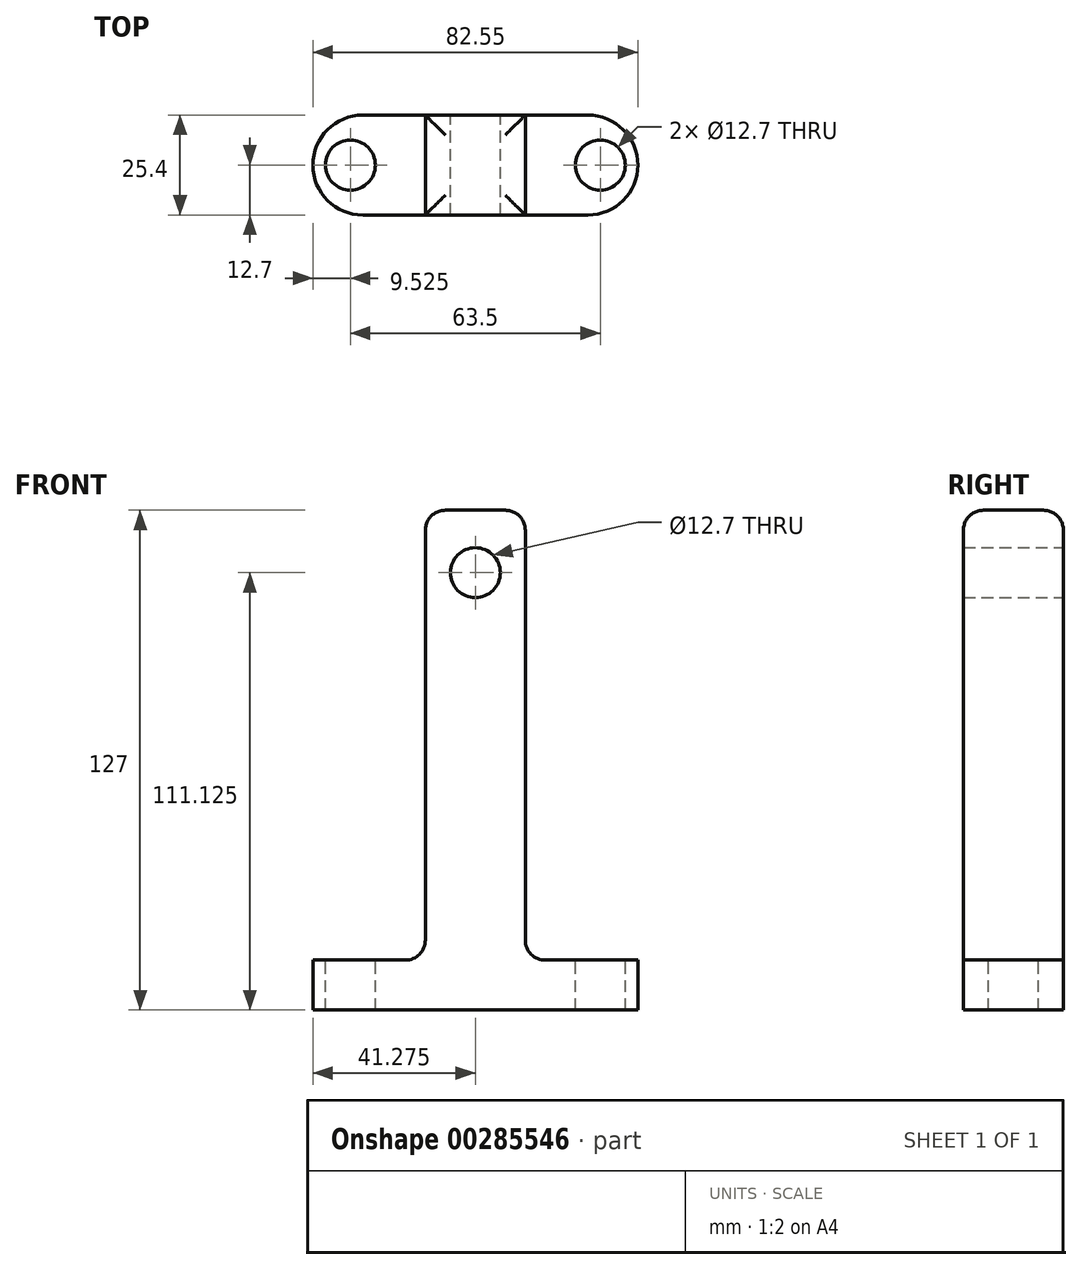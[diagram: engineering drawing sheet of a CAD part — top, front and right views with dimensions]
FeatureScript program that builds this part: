
annotation { "Feature Type Name" : "Feature", "Feature Type Description" : "" }
export const myFeature = defineFeature(function(context is Context, id is Id, definition is map)
    precondition{}
    {
        {
            var Q0;
            Q0=qCreatedBy(makeId("Top.planeOp"),FACE);
            var sketch = newSketch(context, id + "F0", { "sketchPlane" : qUnion([Q0])});
            skLineSegment(sketch, "E0", {"start": v(0, 0) * mm, "end": v(57.15, 0) * mm});
            skLineSegment(sketch, "E1.0", {"start": v(0, -25.4) * mm, "end": v(57.15, -25.4) * mm});
            skArc(sketch, "E2", {"start": v(0, 0) * mm, "mid": v(-12.7, -12.7) * mm, "end": v(0, -25.4) * mm});
            skPoint(sketch, "E2.third.point", {"position": v(12.41, -10) * mm});
            skArc(sketch, "E3", {"start": v(57.15, -25.4) * mm, "mid": v(69.85, -12.7) * mm, "end": v(57.15, 0) * mm});
            skPoint(sketch, "E3.third.point", {"position": v(44.45, -12.67) * mm});
            skLineSegment(sketch, "E4", {"start": v(28.58, 0) * mm, "end": v(28.58, -25.4) * mm, "construction": true});
            skLineSegment(sketch, "E5", {"start": v(15.88, 0) * mm, "end": v(15.88, -25.4) * mm});
            skLineSegment(sketch, "E6.MirrorCS", {"start": v(41.28, 0) * mm, "end": v(41.28, -25.4) * mm});
            skSolve(sketch);
        }
        {
            var Q0;
            Q0 = qSketchRegion(id + "F0", true);
            extrude(context, id + "F1", {"entities" : qUnion([Q0]), "depth" : 12.7 * mm});
        }
        {
            var Q0;
            Q0=qCreatedBy(makeId("Top.planeOp"),FACE);
            cPlane(context, id + "F2", {"entities" : qUnion([Q0]), "cplaneType" : CPlaneType.OFFSET, "offset" : 127 * mm, "width" : 152.4 * mm, "height" : 152.4 * mm});
        }
        {
            var Q0;
            Q0=qCreatedBy(id+"F2.planeOp",FACE);
            var sketch = newSketch(context, id + "F3", { "sketchPlane" : qUnion([Q0])});
            skLineSegment(sketch, "E7", {"start": v(15.88, 0) * mm, "end": v(15.88, -25.4) * mm});
            skPoint(sketch, "E8.orphan", {"position": v(11.05, -22.86) * mm});
            skPoint(sketch, "E9.orphan", {"position": v(15.88, -25.4) * mm});
            skPoint(sketch, "E10.orphan", {"position": v(11.05, -2.54) * mm});
            skPoint(sketch, "E11.orphan", {"position": v(15.88, 0) * mm});
            skLineSegment(sketch, "E12.MirrorCS", {"start": v(41.28, 0) * mm, "end": v(41.28, -25.4) * mm});
            skLineSegment(sketch, "E13", {"start": v(41.28, 0) * mm, "end": v(15.88, 0) * mm});
            skLineSegment(sketch, "E14", {"start": v(15.88, -25.4) * mm, "end": v(41.28, -25.4) * mm});
            skSolve(sketch);
        }
        {
            var Q1;
            {var subQ0=sQuery(id+"F0.wireOp",EDGE,"E5");Q1=makeQuery(id+"F0.imprint","IMPRINT",FACE,{"disambiguationData":[TD([[makeQuery(id+"F0.imprint","IMPRINT",EDGE,{"derivedFrom":subQ0}),1.0]])]});}
            var Q2;
            Q2=makeQuery(id+"F3.imprint","IMPRINT",FACE,{"disambiguationData":[TD([[makeQuery(id+"F3.imprint","IMPRINT",EDGE,{"derivedFrom":sQuery(id+"F3.wireOp",EDGE,"E7")}),1.0]])]});
            loft(context, id + "F4", {"operationType" : NewBodyOperationType.ADD, "sheetProfilesArray" : [{ "sheetProfileEntities" : qUnion([Q1]) }, { "sheetProfileEntities" : qUnion([Q2]) }]});
        }
        {
            var Q0;
            {var subQ0=sQuery(id+"F0.wireOp",EDGE,"E1.0");var subQ1=sQuery(id+"F0.wireOp",EDGE,"E0");Q0=makeQuery(id+"F4.boolean.opBoolean","INTERSECT",EDGE,{"derivedFrom":[makeQuery(id+"F1.opExtrude","CAP_FACE",FACE,{"disambiguationData":[OSD([subQ1,subQ0,sQuery(id+"F0.wireOp",EDGE,"E2"),sQuery(id+"F0.wireOp",EDGE,"E3")])],"isStart":false}),makeQuery(id+"F4.opLoft","SWEPT_FACE",FACE,{"disambiguationData":[OSD([subQ1,subQ0,sQuery(id+"F0.wireOp",EDGE,"E6.MirrorCS"),sQuery(id+"F3.wireOp",EDGE,"E12.MirrorCS"),sQuery(id+"F3.wireOp",EDGE,"E13"),sQuery(id+"F3.wireOp",EDGE,"E14")])]})]});}
            var Q1;
            {var subQ0=sQuery(id+"F0.wireOp",EDGE,"E1.0");var subQ1=sQuery(id+"F0.wireOp",EDGE,"E0");Q1=makeQuery(id+"F4.boolean.opBoolean","INTERSECT",EDGE,{"derivedFrom":[makeQuery(id+"F1.opExtrude","CAP_FACE",FACE,{"disambiguationData":[OSD([subQ1,subQ0,sQuery(id+"F0.wireOp",EDGE,"E2"),sQuery(id+"F0.wireOp",EDGE,"E3")])],"isStart":false}),makeQuery(id+"F4.opLoft","SWEPT_FACE",FACE,{"disambiguationData":[OSD([subQ1,subQ0,sQuery(id+"F0.wireOp",EDGE,"E5"),sQuery(id+"F3.wireOp",EDGE,"E7"),sQuery(id+"F3.wireOp",EDGE,"E13"),sQuery(id+"F3.wireOp",EDGE,"E14")])]})]});}
            var Q2;
            Q2=makeQuery(id+"F4.opLoft","MID_CAP_EDGE",EDGE,{"disambiguationData":[OSD([sQuery(id+"F3.wireOp",EDGE,"E7"),sQuery(id+"F3.wireOp",EDGE,"E12.MirrorCS"),sQuery(id+"F3.wireOp",EDGE,"E13")])],"capPos":1.0});
            var Q3;
            Q3=makeQuery(id+"F4.opLoft","CAP_FACE",FACE,{"disambiguationData":[OSD([makeQuery(id+"F3.imprint","IMPRINT",FACE,{"disambiguationData":[TD([[makeQuery(id+"F3.imprint","IMPRINT",EDGE,{"derivedFrom":sQuery(id+"F3.wireOp",EDGE,"E7")}),1.0]])]})])],"isStart":true});
            fillet(context, id + "F5", {"entities" : qUnion([Q0, Q1, Q2, Q3]), "radius" : 5.08 * mm, "tangentPropagation" : true, "allowEdgeOverflow" : false});
        }
        {
            var Q0;
            Q0=qCreatedBy(makeId("Front.planeOp"),FACE);
            var sketch = newSketch(context, id + "F6", { "sketchPlane" : qUnion([Q0])});
            skPoint(sketch, "E15", {"position": v(0, 111.13) * mm});
            skPoint(sketch, "E16", {"position": v(28.57, 111.13) * mm});
            skSolve(sketch);
        }
        {
            var Q0;
            Q0=sQuery(id+"F6.wireOp",VERTEX,"E16");
            var Q1;
            Q1=makeQuery(id+"F1.opExtrude","SWEPT_BODY",BODY,{"disambiguationData":[OSD([sQuery(id+"F0.wireOp",EDGE,"E0"),sQuery(id+"F0.wireOp",EDGE,"E1.0"),sQuery(id+"F0.wireOp",EDGE,"E2"),sQuery(id+"F0.wireOp",EDGE,"E3")])]});
            hole(context, id + "F7", {"style" : HoleStyle.SIMPLE, "endStyle" : HoleEndStyle.BLIND, "oppositeDirection" : true, "holeDiameter" : 12.7 * mm, "holeDepth" : 25.4 * mm, "tappedDepth" : 12.7 * mm, "tapClearance" : 3, "locations" : qUnion([Q0]), "scope" : qUnion([Q1])});
        }
        {
            var Q0;
            {var subQ0=sQuery(id+"F0.wireOp",EDGE,"E2");var subQ1=sQuery(id+"F0.wireOp",EDGE,"E1.0");var subQ6=sQuery(id+"F0.wireOp",EDGE,"E0");Q0=makeQuery(id+"F4.boolean.opBoolean","SPLIT",FACE,{"disambiguationData":[TD([makeQuery(id+"F1.opExtrude","SWEPT_FACE",FACE,{"disambiguationData":[OSD([subQ0])]})])],"derivedFrom":makeQuery(id+"F1.opExtrude","CAP_FACE",FACE,{"disambiguationData":[OSD([subQ6,subQ1,subQ0,sQuery(id+"F0.wireOp",EDGE,"E3")])],"isStart":false})});}
            var sketch = newSketch(context, id + "F8", { "sketchPlane" : qUnion([Q0])});
            skPoint(sketch, "E17", {"position": v(60.33, -12.7) * mm});
            skPoint(sketch, "E18", {"position": v(-3.18, -12.7) * mm});
            skSolve(sketch);
        }
        {
            var Q0;
            Q0=sQuery(id+"F8.wireOp",VERTEX,"E18");
            var Q1;
            Q1=sQuery(id+"F8.wireOp",VERTEX,"E17");
            var Q2;
            Q2=makeQuery(id+"F1.opExtrude","SWEPT_BODY",BODY,{"disambiguationData":[OSD([sQuery(id+"F0.wireOp",EDGE,"E0"),sQuery(id+"F0.wireOp",EDGE,"E1.0"),sQuery(id+"F0.wireOp",EDGE,"E2"),sQuery(id+"F0.wireOp",EDGE,"E3")])]});
            hole(context, id + "F9", {"style" : HoleStyle.SIMPLE, "endStyle" : HoleEndStyle.BLIND, "holeDiameter" : 12.7 * mm, "holeDepth" : 25.4 * mm, "tappedDepth" : 12.7 * mm, "tapClearance" : 3, "locations" : qUnion([Q0, Q1]), "scope" : qUnion([Q2])});
        }
    });
